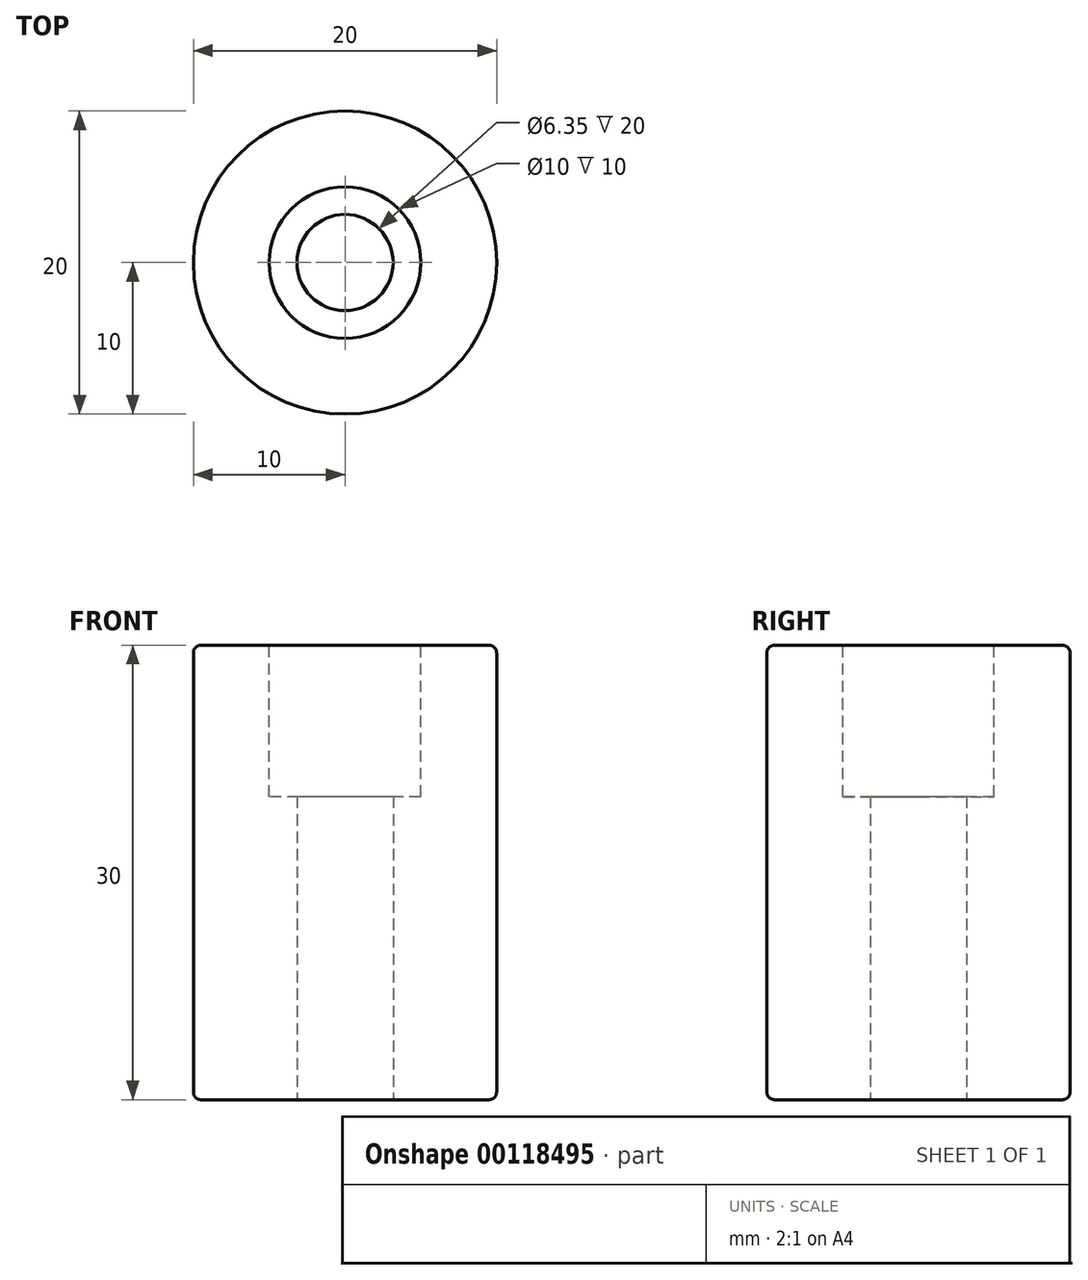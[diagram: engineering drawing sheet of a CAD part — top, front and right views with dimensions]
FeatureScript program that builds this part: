
annotation { "Feature Type Name" : "Feature", "Feature Type Description" : "" }
export const myFeature = defineFeature(function(context is Context, id is Id, definition is map)
    precondition{}
    {
        {
            var Q0;
            Q0=qCreatedBy(makeId("Top.planeOp"),FACE);
            var sketch = newSketch(context, id + "F0", { "sketchPlane" : qUnion([Q0])});
            skCircle(sketch, "E0", {"center": v(0, 0) * mm, "radius": 10 * mm});
            skCircle(sketch, "E1", {"center": v(0, 0) * mm, "radius": 3.18 * mm});
            skSolve(sketch);
        }
        {
            var Q0;
            Q0=makeQuery(id+"F0.imprint","IMPRINT",FACE,{"disambiguationData":[TD([[makeQuery(id+"F0.imprint","IMPRINT",EDGE,{"derivedFrom":sQuery(id+"F0.wireOp",EDGE,"E0")}),1.0]])]});
            extrude(context, id + "F1", {"entities" : qUnion([Q0]), "depth" : 30 * mm, "symmetric" : true});
        }
        {
            var Q0;
            Q0=makeQuery(id+"F1.opExtrude","CAP_FACE",FACE,{"disambiguationData":[OSD([sQuery(id+"F0.wireOp",EDGE,"E0"),sQuery(id+"F0.wireOp",EDGE,"E1")])],"isStart":false});
            var sketch = newSketch(context, id + "F2", { "sketchPlane" : qUnion([Q0])});
            skCircle(sketch, "E2", {"center": v(0, 0) * mm, "radius": 5 * mm});
            skSolve(sketch);
        }
        {
            var Q0;
            Q0 = qSketchRegion(id + "F2", true);
            extrude(context, id + "F3", {"entities" : qUnion([Q0]), "operationType" : NewBodyOperationType.REMOVE, "oppositeDirection" : true, "depth" : 10 * mm});
        }
        {
            var Q0;
            Q0=makeQuery(id+"F1.opExtrude","CAP_EDGE",EDGE,{"disambiguationData":[OSD([sQuery(id+"F0.wireOp",EDGE,"E0")])],"isStart":false});
            var Q1;
            Q1=makeQuery(id+"F1.opExtrude","CAP_EDGE",EDGE,{"disambiguationData":[OSD([sQuery(id+"F0.wireOp",EDGE,"E0")])],"isStart":true});
            fillet(context, id + "F4", {"entities" : qUnion([Q0, Q1]), "radius" : 0.5 * mm, "tangentPropagation" : true, "allowEdgeOverflow" : false});
        }
    });
